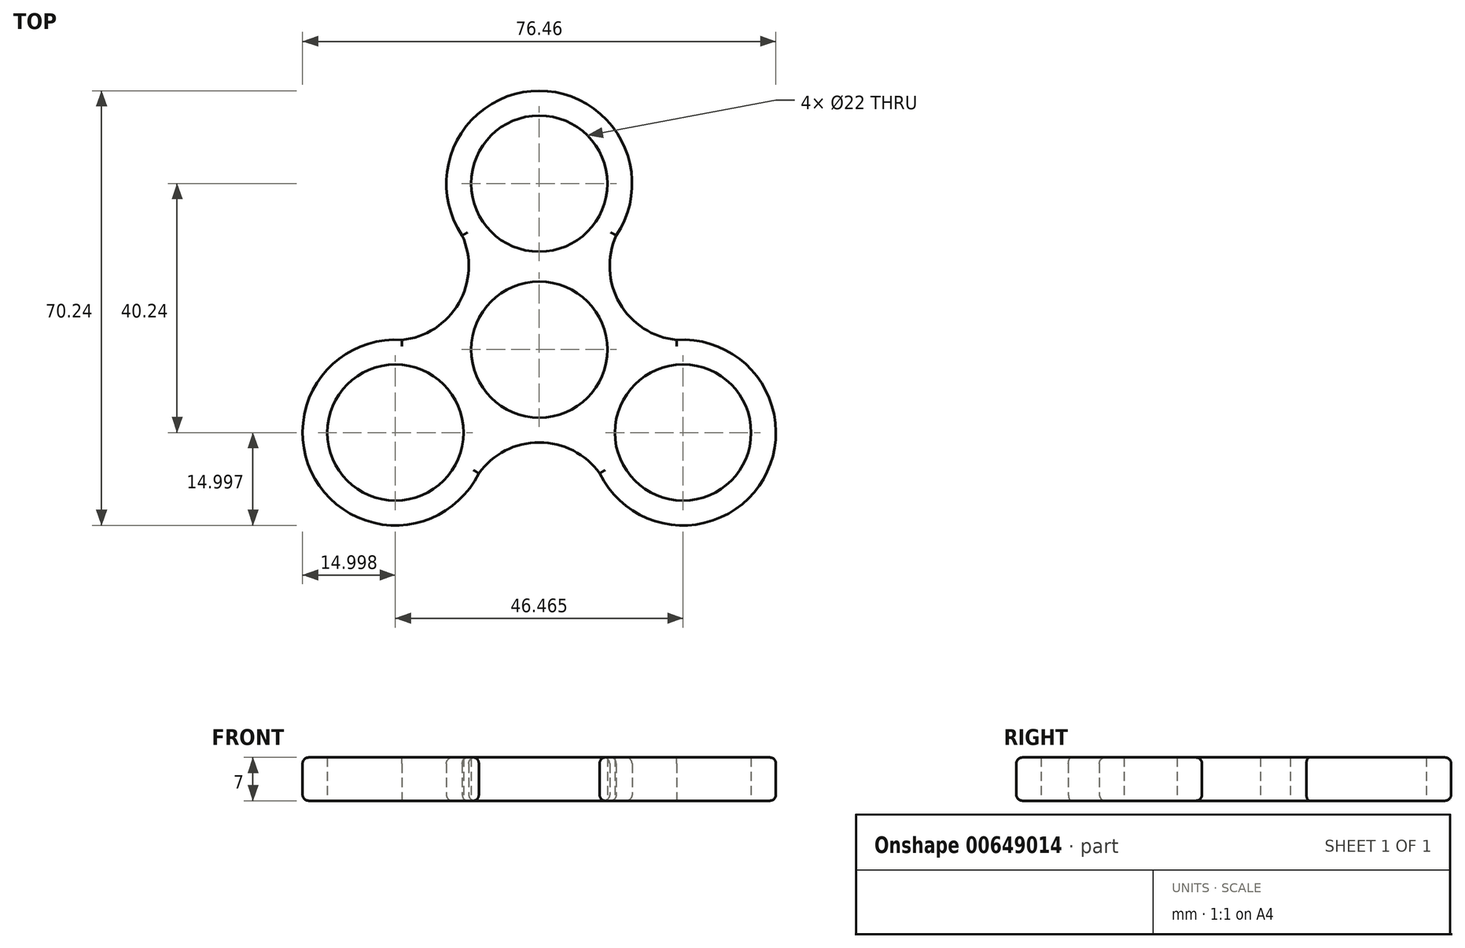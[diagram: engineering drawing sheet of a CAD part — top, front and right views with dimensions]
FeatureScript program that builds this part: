
annotation { "Feature Type Name" : "Feature", "Feature Type Description" : "" }
export const myFeature = defineFeature(function(context is Context, id is Id, definition is map)
    precondition{}
    {
        {
            var Q0;
            Q0=qCreatedBy(makeId("Top.planeOp"),FACE);
            var sketch = newSketch(context, id + "F0", { "sketchPlane" : qUnion([Q0])});
            skLineSegment(sketch, "E0", {"start": v(0, 0) * mm, "end": v(0, 26.83) * mm});
            skLineSegment(sketch, "E1", {"start": v(0, 0) * mm, "end": v(23.23, -13.41) * mm});
            skLineSegment(sketch, "E2", {"start": v(0, 0) * mm, "end": v(-23.23, -13.41) * mm});
            skCircle(sketch, "E3", {"center": v(-23.23, -13.41) * mm, "radius": 11 * mm});
            skCircle(sketch, "E4", {"center": v(23.23, -13.41) * mm, "radius": 11 * mm});
            skCircle(sketch, "E5", {"center": v(0, 26.83) * mm, "radius": 11 * mm});
            skCircle(sketch, "E6", {"center": v(0, 0) * mm, "radius": 11 * mm});
            skCircle(sketch, "E7", {"center": v(-23.23, -13.41) * mm, "radius": 15 * mm});
            skCircle(sketch, "E8", {"center": v(23.23, -13.41) * mm, "radius": 15 * mm});
            skCircle(sketch, "E9", {"center": v(0, 26.83) * mm, "radius": 15 * mm});
            skPoint(sketch, "E10", {"position": v(0, 41.83) * mm});
            skLineSegment(sketch, "E11", {"start": v(-8.83, 14.7) * mm, "end": v(-17.15, 0.3) * mm});
            skLineSegment(sketch, "E12", {"start": v(8.83, 14.7) * mm, "end": v(17.15, 0.3) * mm});
            skLineSegment(sketch, "E13", {"start": v(8.32, -15) * mm, "end": v(-8.32, -15) * mm});
            skArc(sketch, "E14", {"start": v(-22.2, 1.55) * mm, "mid": v(-13, 7.5) * mm, "end": v(-12.44, 18.45) * mm});
            skLineSegment(sketch, "E15", {"start": v(-22.2, 1.55) * mm, "end": v(-12.44, 18.45) * mm});
            skArc(sketch, "E16", {"start": v(12.44, 18.45) * mm, "mid": v(13, 7.5) * mm, "end": v(22.2, 1.55) * mm});
            skArc(sketch, "E17", {"start": v(9.76, -20) * mm, "mid": v(0, -15) * mm, "end": v(-9.76, -20) * mm});
            skLineSegment(sketch, "E18", {"start": v(-9.76, -20) * mm, "end": v(9.76, -20) * mm});
            skLineSegment(sketch, "E19", {"start": v(12.44, 18.45) * mm, "end": v(22.2, 1.55) * mm});
            skSolve(sketch);
        }
        {
            var Q0;
            {var subQ0=sQuery(id+"F0.wireOp",EDGE,"E11");var subQ1=sQuery(id+"F0.wireOp",EDGE,"E7");var subQ2=makeQuery(id+"F0.imprint","INTERSECT",VERTEX,{"derivedFrom":[subQ1,subQ0]});Q0=makeQuery(id+"F0.imprint","IMPRINT",FACE,{"disambiguationData":[TD([[makeQuery(id+"F0.imprint","IMPRINT",EDGE,{"disambiguationData":[TD([[subQ2,1.0]])],"derivedFrom":subQ0}),-1.0]])]});}
            var Q1;
            {var subQ0=sQuery(id+"F0.wireOp",EDGE,"E13");var subQ1=sQuery(id+"F0.wireOp",EDGE,"E7");var subQ2=makeQuery(id+"F0.imprint","INTERSECT",VERTEX,{"derivedFrom":[subQ1,subQ0]});Q1=makeQuery(id+"F0.imprint","IMPRINT",FACE,{"disambiguationData":[TD([[makeQuery(id+"F0.imprint","IMPRINT",EDGE,{"disambiguationData":[TD([[subQ2,1.0]])],"derivedFrom":subQ0}),1.0]])]});}
            var Q2;
            {var subQ0=sQuery(id+"F0.wireOp",EDGE,"E12");var subQ1=sQuery(id+"F0.wireOp",EDGE,"E8");var subQ2=makeQuery(id+"F0.imprint","INTERSECT",VERTEX,{"derivedFrom":[subQ1,subQ0]});Q2=makeQuery(id+"F0.imprint","IMPRINT",FACE,{"disambiguationData":[TD([[makeQuery(id+"F0.imprint","IMPRINT",EDGE,{"disambiguationData":[TD([[subQ2,1.0]])],"derivedFrom":subQ0}),1.0]])]});}
            var Q3;
            {var subQ0=sQuery(id+"F0.wireOp",EDGE,"E13");var subQ1=sQuery(id+"F0.wireOp",EDGE,"E8");var subQ2=makeQuery(id+"F0.imprint","INTERSECT",VERTEX,{"derivedFrom":[subQ1,subQ0]});Q3=makeQuery(id+"F0.imprint","IMPRINT",FACE,{"disambiguationData":[TD([[makeQuery(id+"F0.imprint","IMPRINT",EDGE,{"disambiguationData":[TD([[subQ2,-1.0]])],"derivedFrom":subQ0}),1.0]])]});}
            var Q4;
            {var subQ0=sQuery(id+"F0.wireOp",EDGE,"E11");var subQ1=sQuery(id+"F0.wireOp",EDGE,"E9");var subQ2=makeQuery(id+"F0.imprint","INTERSECT",VERTEX,{"derivedFrom":[subQ1,subQ0]});Q4=makeQuery(id+"F0.imprint","IMPRINT",FACE,{"disambiguationData":[TD([[makeQuery(id+"F0.imprint","IMPRINT",EDGE,{"disambiguationData":[TD([[subQ2,-1.0]])],"derivedFrom":subQ0}),-1.0]])]});}
            var Q5;
            {var subQ0=sQuery(id+"F0.wireOp",EDGE,"E12");var subQ1=sQuery(id+"F0.wireOp",EDGE,"E9");var subQ2=makeQuery(id+"F0.imprint","INTERSECT",VERTEX,{"derivedFrom":[subQ1,subQ0]});Q5=makeQuery(id+"F0.imprint","IMPRINT",FACE,{"disambiguationData":[TD([[makeQuery(id+"F0.imprint","IMPRINT",EDGE,{"disambiguationData":[TD([[subQ2,-1.0]])],"derivedFrom":subQ0}),1.0]])]});}
            var Q6;
            Q6=makeQuery(id+"F0.imprint","IMPRINT",FACE,{"disambiguationData":[TD([[makeQuery(id+"F0.imprint","IMPRINT",EDGE,{"derivedFrom":sQuery(id+"F0.wireOp",EDGE,"E3")}),-1.0]])]});
            var Q7;
            Q7=makeQuery(id+"F0.imprint","IMPRINT",FACE,{"disambiguationData":[TD([[makeQuery(id+"F0.imprint","IMPRINT",EDGE,{"derivedFrom":sQuery(id+"F0.wireOp",EDGE,"E4")}),-1.0]])]});
            var Q8;
            Q8=makeQuery(id+"F0.imprint","IMPRINT",FACE,{"disambiguationData":[TD([[makeQuery(id+"F0.imprint","IMPRINT",EDGE,{"derivedFrom":sQuery(id+"F0.wireOp",EDGE,"E5")}),-1.0]])]});
            var Q9;
            {var subQ7=sQuery(id+"F0.wireOp",EDGE,"E1");var subQ10=sQuery(id+"F0.wireOp",EDGE,"E8");var subQ11=makeQuery(id+"F0.imprint","INTERSECT",VERTEX,{"derivedFrom":[subQ7,subQ10]});Q9=makeQuery(id+"F0.imprint","IMPRINT",FACE,{"disambiguationData":[TD([[makeQuery(id+"F0.imprint","IMPRINT",EDGE,{"disambiguationData":[TD([[subQ11,1.0]])],"derivedFrom":subQ7}),-1.0]])]});}
            var Q10;
            {var subQ5=sQuery(id+"F0.wireOp",EDGE,"E9");var subQ10=sQuery(id+"F0.wireOp",EDGE,"E0");var subQ12=makeQuery(id+"F0.imprint","INTERSECT",VERTEX,{"derivedFrom":[subQ10,subQ5]});Q10=makeQuery(id+"F0.imprint","IMPRINT",FACE,{"disambiguationData":[TD([[makeQuery(id+"F0.imprint","IMPRINT",EDGE,{"disambiguationData":[TD([[subQ12,1.0]])],"derivedFrom":subQ10}),-1.0]])]});}
            var Q11;
            {var subQ5=sQuery(id+"F0.wireOp",EDGE,"E9");var subQ6=sQuery(id+"F0.wireOp",EDGE,"E0");var subQ7=makeQuery(id+"F0.imprint","INTERSECT",VERTEX,{"derivedFrom":[subQ6,subQ5]});Q11=makeQuery(id+"F0.imprint","IMPRINT",FACE,{"disambiguationData":[TD([[makeQuery(id+"F0.imprint","IMPRINT",EDGE,{"disambiguationData":[TD([[subQ7,1.0]])],"derivedFrom":subQ6}),1.0]])]});}
            extrude(context, id + "F1", {"entities" : qUnion([Q0, Q1, Q2, Q3, Q4, Q5, Q6, Q7, Q8, Q9, Q10, Q11]), "depth" : 7 * mm, "offsetDistance" : 25 * mm});
        }
        {
            var Q0;
            Q0=makeQuery(id+"F1.opExtrude","CAP_EDGE",EDGE,{"disambiguationData":[OSD([sQuery(id+"F0.wireOp",EDGE,"E14")])],"isStart":false});
            var Q1;
            Q1=makeQuery(id+"F1.opExtrude","CAP_EDGE",EDGE,{"disambiguationData":[OSD([sQuery(id+"F0.wireOp",EDGE,"E16")])],"isStart":false});
            var Q2;
            Q2=makeQuery(id+"F1.opExtrude","CAP_EDGE",EDGE,{"disambiguationData":[OSD([sQuery(id+"F0.wireOp",EDGE,"E17")])],"isStart":false});
            var Q3;
            Q3=makeQuery(id+"F1.opExtrude","CAP_EDGE",EDGE,{"disambiguationData":[OSD([sQuery(id+"F0.wireOp",EDGE,"E7")])],"isStart":false});
            var Q4;
            Q4=makeQuery(id+"F1.opExtrude","CAP_EDGE",EDGE,{"disambiguationData":[OSD([sQuery(id+"F0.wireOp",EDGE,"E8")])],"isStart":false});
            var Q5;
            Q5=makeQuery(id+"F1.opExtrude","CAP_EDGE",EDGE,{"disambiguationData":[OSD([sQuery(id+"F0.wireOp",EDGE,"E9")])],"isStart":false});
            fillet(context, id + "F2", {"entities" : qUnion([Q0, Q1, Q2, Q3, Q4, Q5]), "radius" : 1 * mm, "tangentPropagation" : true, "allowEdgeOverflow" : false});
        }
        {
            var Q0;
            Q0=makeQuery(id+"F1.opExtrude","CAP_EDGE",EDGE,{"disambiguationData":[OSD([sQuery(id+"F0.wireOp",EDGE,"E16")])],"isStart":true});
            var Q1;
            Q1=makeQuery(id+"F1.opExtrude","CAP_EDGE",EDGE,{"disambiguationData":[OSD([sQuery(id+"F0.wireOp",EDGE,"E17")])],"isStart":true});
            var Q2;
            Q2=makeQuery(id+"F1.opExtrude","CAP_EDGE",EDGE,{"disambiguationData":[OSD([sQuery(id+"F0.wireOp",EDGE,"E8")])],"isStart":true});
            var Q3;
            Q3=makeQuery(id+"F1.opExtrude","CAP_EDGE",EDGE,{"disambiguationData":[OSD([sQuery(id+"F0.wireOp",EDGE,"E7")])],"isStart":true});
            var Q4;
            Q4=makeQuery(id+"F1.opExtrude","CAP_EDGE",EDGE,{"disambiguationData":[OSD([sQuery(id+"F0.wireOp",EDGE,"E14")])],"isStart":true});
            var Q5;
            Q5=makeQuery(id+"F1.opExtrude","CAP_EDGE",EDGE,{"disambiguationData":[OSD([sQuery(id+"F0.wireOp",EDGE,"E9")])],"isStart":true});
            fillet(context, id + "F3", {"entities" : qUnion([Q0, Q1, Q2, Q3, Q4, Q5]), "radius" : 1 * mm, "tangentPropagation" : true, "allowEdgeOverflow" : false});
        }
    });
